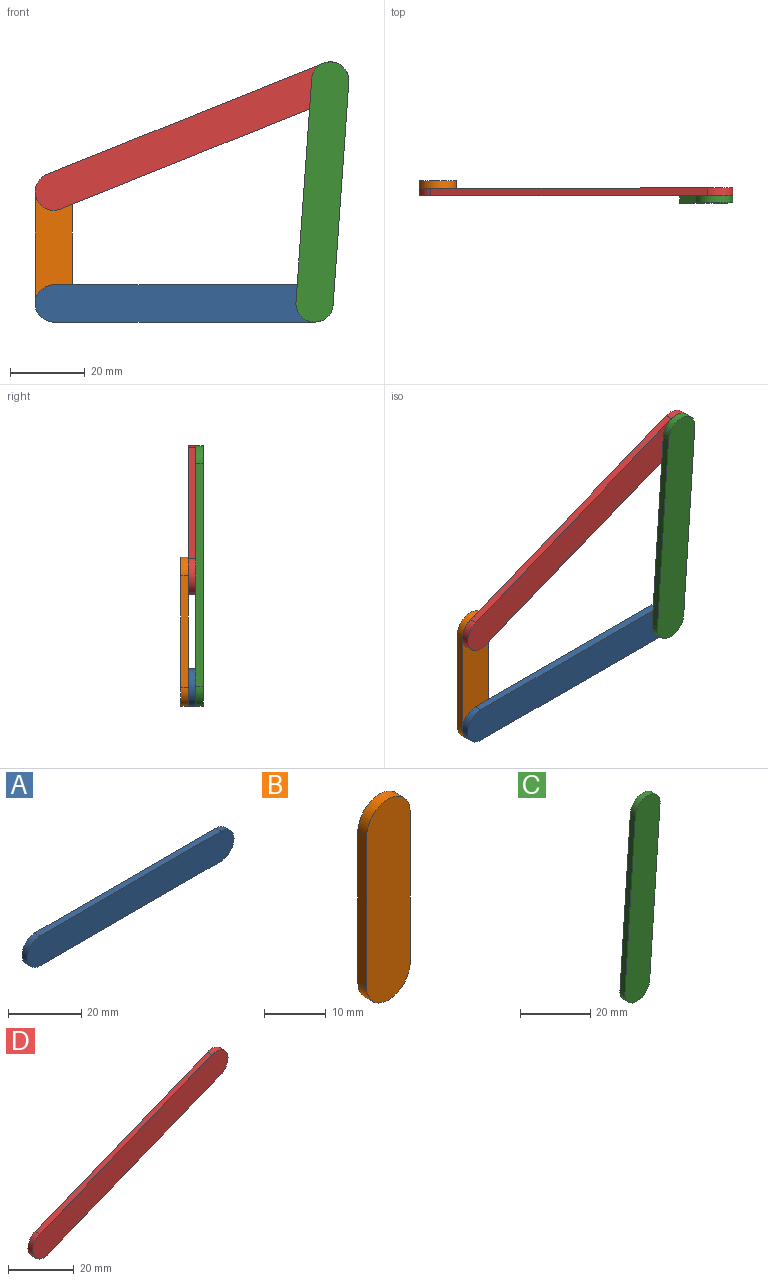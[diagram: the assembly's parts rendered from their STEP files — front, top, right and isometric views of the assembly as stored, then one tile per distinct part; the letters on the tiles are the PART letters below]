
ASSEMBLY  parts=4 mates=4
PART A: 6 faces, bbox 80x2x10 mm
  f0: cylinder r=5mm len=10mm, axis (0,1,0), area 31.4mm2, adj f1,f3,f4,f5
  f1: plane 70x2mm, normal (0,0,1), area 140mm2, adj f0,f2,f4,f5
  f2: cylinder r=5mm len=10mm, axis (0,1,0), area 31.4mm2, adj f1,f3,f4,f5
  f3: plane 70x2mm, normal (0,0,-1), area 140mm2, adj f0,f2,f4,f5
  f4: plane 80x10mm, normal (0,-1,0), area 778.5mm2, adj f0,f1,f2,f3
  f5: plane 80x10mm, normal (0,1,0), area 778.5mm2, adj f0,f1,f2,f3
PART B: 6 faces, bbox 10x2x40 mm
  f0: cylinder r=5mm len=10mm, axis (0,-1,0), area 31.4mm2, adj f1,f3,f4,f5
  f1: plane 30x2mm, normal (-1,0,0), area 60mm2, adj f0,f2,f4,f5
  f2: cylinder r=5mm len=10mm, axis (0,-1,0), area 31.4mm2, adj f1,f3,f4,f5
  f3: plane 30x2mm, normal (1,0,0), area 60mm2, adj f0,f2,f4,f5
  f4: plane 40x10mm, normal (0,1,0), area 378.5mm2, adj f0,f1,f2,f3
  f5: plane 40x10mm, normal (0,-1,0), area 378.5mm2, adj f0,f1,f2,f3
PART C: 6 faces, bbox 14.2x2x69.9 mm
  f0: cylinder r=5mm len=9.99mm, axis (0,1,0), area 31.4mm2, adj f1,f3,f4,f5
  f1: plane 59.85x4.22mm, normal (1,0,-0.07), area 120mm2, adj f0,f2,f4,f5
  f2: cylinder r=5mm len=9.99mm, axis (0,1,0), area 31.4mm2, adj f1,f3,f4,f5
  f3: plane 59.85x4.22mm, normal (-1,0,0.07), area 120mm2, adj f0,f2,f4,f5
  f4: plane 69.85x14.22mm, normal (0,-1,0), area 678.5mm2, adj f0,f1,f2,f3
  f5: plane 69.85x14.22mm, normal (0,1,0), area 678.5mm2, adj f0,f1,f2,f3
PART D: 6 faces, bbox 84.2x2x39.9 mm
  f0: cylinder r=5mm len=9.64mm, axis (0,1,0), area 31.4mm2, adj f1,f3,f4,f5
  f1: plane 74.22x29.85mm, normal (0.37,0,-0.93), area 160mm2, adj f0,f2,f4,f5
  f2: cylinder r=5mm len=9.64mm, axis (0,1,0), area 31.4mm2, adj f1,f3,f4,f5
  f3: plane 74.22x29.85mm, normal (-0.37,0,0.93), area 160mm2, adj f0,f2,f4,f5
  f4: plane 84.22x39.85mm, normal (0,-1,0), area 878.5mm2, adj f0,f1,f2,f3
  f5: plane 84.22x39.85mm, normal (0,1,0), area 878.5mm2, adj f0,f1,f2,f3
PLACE A at identity
PLACE B at identity
PLACE C at identity fixed
PLACE D at identity
MATE revolute B.f0 <-> A.f2  axis (0,-1,0) through (-35,0,0)mm
MATE revolute A.f0 <-> C.f0  axis (0,-1,0) through (35,-2,0)mm
MATE revolute B.f2 <-> D.f0  axis (0,-1,0) through (-35,0,30)mm
MATE revolute C.f2 <-> D.f2  axis (0,1,0) through (39.22,-2,59.85)mm
